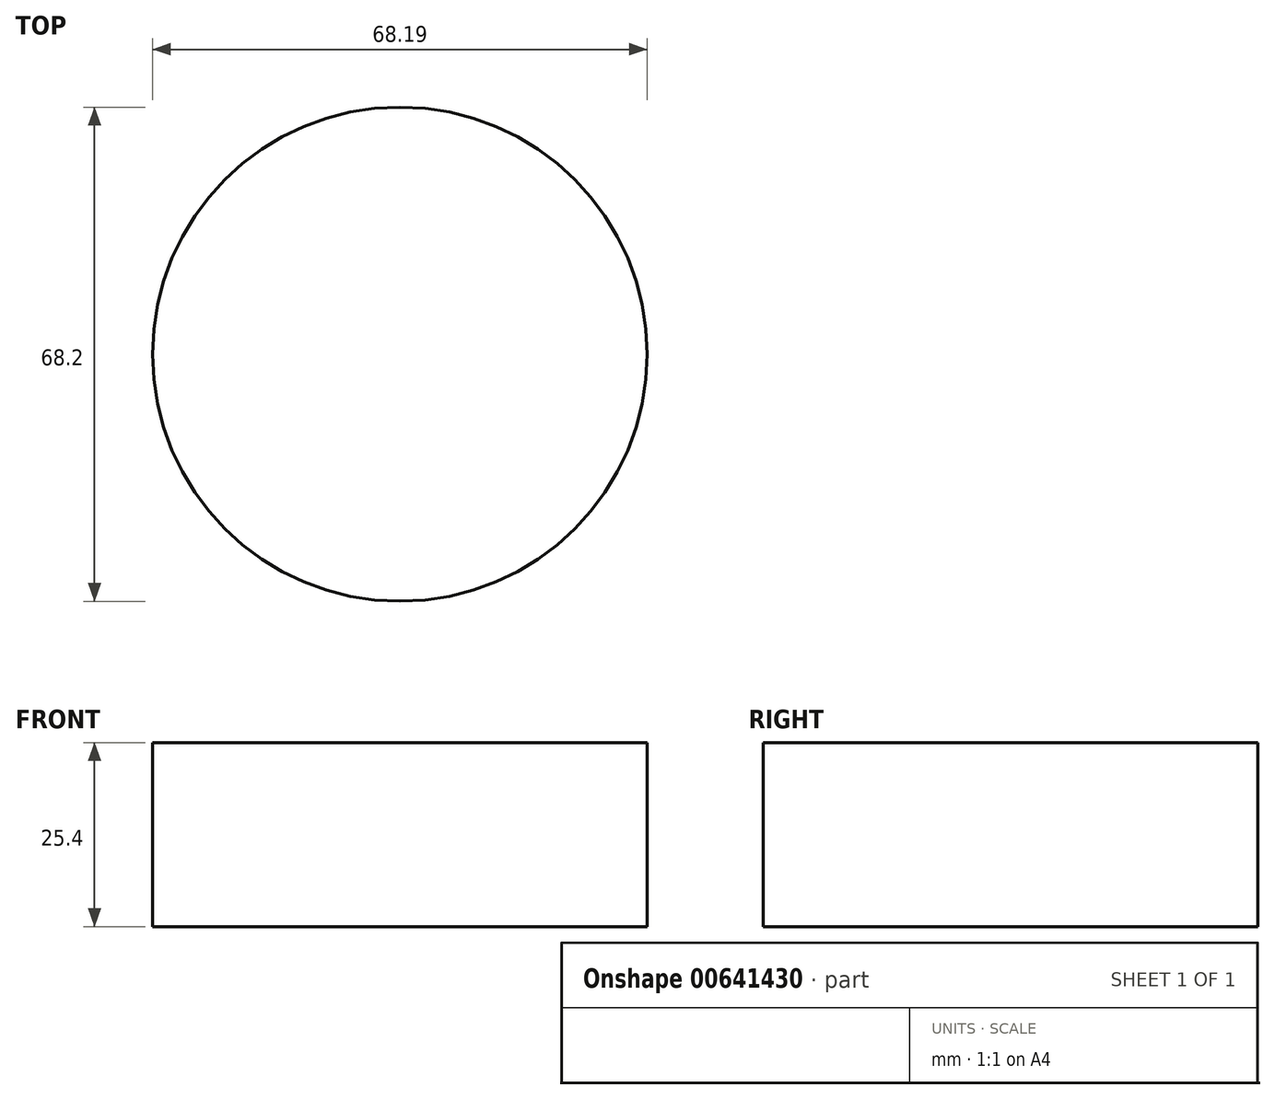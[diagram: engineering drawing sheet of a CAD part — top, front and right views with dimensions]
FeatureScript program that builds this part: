
annotation { "Feature Type Name" : "Feature", "Feature Type Description" : "" }
export const myFeature = defineFeature(function(context is Context, id is Id, definition is map)
    precondition{}
    {
        {
            var Q0;
            Q0=qCreatedBy(makeId("Top.planeOp"),FACE);
            var sketch = newSketch(context, id + "F0", { "sketchPlane" : qUnion([Q0])});
            skCircle(sketch, "E0", {"center": v(34.1, 0) * mm, "radius": 34.1 * mm});
            skSolve(sketch);
        }
        {
            var Q0;
            Q0 = qSketchRegion(id + "F0", true);
            extrude(context, id + "F1", {"entities" : qUnion([Q0]), "depth" : 25.4 * mm, "offsetDistance" : 25.4 * mm});
        }
    });
